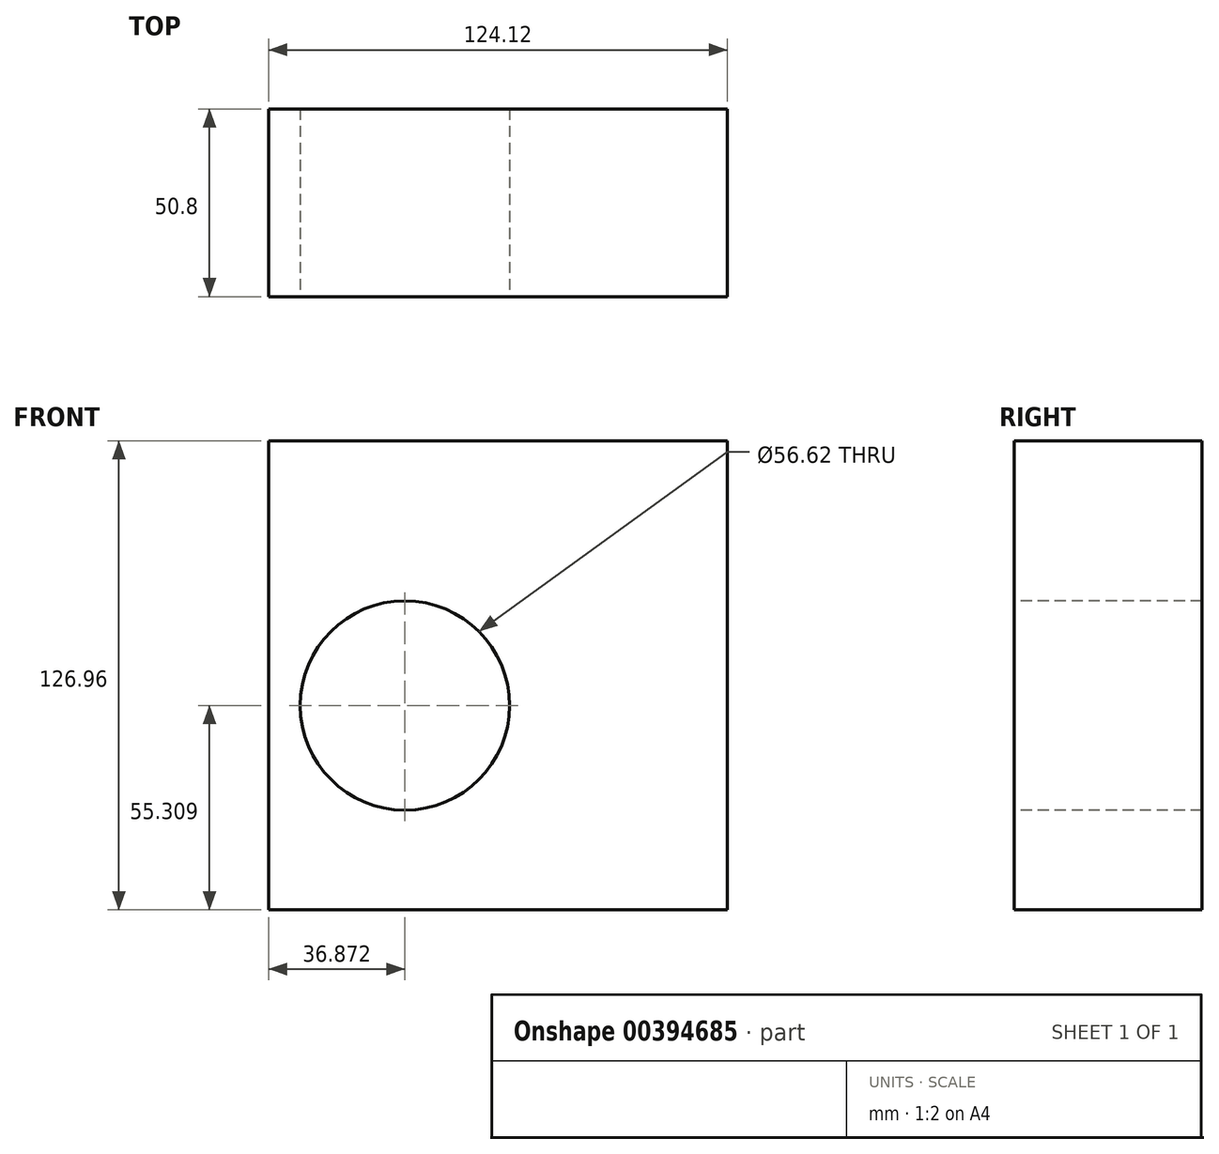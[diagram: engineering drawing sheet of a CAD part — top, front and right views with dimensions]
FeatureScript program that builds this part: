
annotation { "Feature Type Name" : "Feature", "Feature Type Description" : "" }
export const myFeature = defineFeature(function(context is Context, id is Id, definition is map)
    precondition{}
    {
        {
            var Q0;
            Q0=qCreatedBy(makeId("Front.planeOp"),FACE);
            var sketch = newSketch(context, id + "F0", { "sketchPlane" : qUnion([Q0])});
            skLineSegment(sketch, "E0.bottom", {"start": v(-62.06, 63.48) * mm, "end": v(62.06, 63.48) * mm});
            skLineSegment(sketch, "E0.top", {"start": v(-62.06, -63.48) * mm, "end": v(62.06, -63.48) * mm});
            skLineSegment(sketch, "E0.left", {"start": v(-62.06, 63.48) * mm, "end": v(-62.06, -63.48) * mm});
            skLineSegment(sketch, "E0.right", {"start": v(62.06, 63.48) * mm, "end": v(62.06, -63.48) * mm});
            skPoint(sketch, "E0.middle", {"position": v(0, 0) * mm});
            skSolve(sketch);
        }
        {
            var Q0;
            Q0=makeQuery(id+"F0.imprint","IMPRINT",FACE,{"disambiguationData":[TD([[makeQuery(id+"F0.imprint","IMPRINT",EDGE,{"derivedFrom":sQuery(id+"F0.wireOp",EDGE,"E0.bottom")}),-1.0]])]});
            extrude(context, id + "F1", {"entities" : qUnion([Q0]), "depth" : 76.2 * mm});
        }
        {
            var Q0;
            Q0=makeQuery(id+"F1.opExtrude","CAP_FACE",FACE,{"disambiguationData":[OSD([sQuery(id+"F0.wireOp",EDGE,"E0.bottom"),sQuery(id+"F0.wireOp",EDGE,"E0.top"),sQuery(id+"F0.wireOp",EDGE,"E0.left"),sQuery(id+"F0.wireOp",EDGE,"E0.right")])],"isStart":false});
            var sketch = newSketch(context, id + "F2", { "sketchPlane" : qUnion([Q0])});
            skCircle(sketch, "E1", {"center": v(-35.7, 36.61) * mm, "radius": 13.58 * mm});
            skCircle(sketch, "E2", {"center": v(0, 34.1) * mm, "radius": 8.09 * mm});
            skCircle(sketch, "E3", {"center": v(-25.19, -8.17) * mm, "radius": 28.31 * mm});
            skCircle(sketch, "E4", {"center": v(22.97, -9.2) * mm, "radius": 12.11 * mm});
            skCircle(sketch, "E5", {"center": v(34.5, 29.07) * mm, "radius": 23.09 * mm});
            skCircle(sketch, "E6", {"center": v(-44.86, -50.47) * mm, "radius": 6.88 * mm});
            skCircle(sketch, "E7", {"center": v(-14.68, -53.63) * mm, "radius": 4.76 * mm});
            skCircle(sketch, "E8", {"center": v(28.4, -47.3) * mm, "radius": 13.92 * mm});
            skCircle(sketch, "E9", {"center": v(50.78, -20.5) * mm, "radius": 8.55 * mm});
            skCircle(sketch, "E10", {"center": v(69.77, 53.83) * mm, "radius": 10.85 * mm});
            skCircle(sketch, "E11", {"center": v(94.52, 26.39) * mm, "radius": 10.15 * mm});
            skCircle(sketch, "E12", {"center": v(73.16, -1.48) * mm, "radius": 7.82 * mm});
            skCircle(sketch, "E13", {"center": v(77.57, -27.68) * mm, "radius": 2.6 * mm});
            skCircle(sketch, "E14", {"center": v(90.12, -8.12) * mm, "radius": 1.63 * mm});
            skCircle(sketch, "E15", {"center": v(93.85, 46.54) * mm, "radius": 1.66 * mm});
            skCircle(sketch, "E16", {"center": v(72.14, 32.47) * mm, "radius": 8.89 * mm});
            skCircle(sketch, "E17", {"center": v(88.08, 68.27) * mm, "radius": 9.28 * mm});
            skSolve(sketch);
        }
        {
            var Q0;
            Q0=makeQuery(id+"F2.imprint","IMPRINT",FACE,{"disambiguationData":[TD([[makeQuery(id+"F2.imprint","IMPRINT",EDGE,{"derivedFrom":sQuery(id+"F2.wireOp",EDGE,"E3")}),1.0]])]});
            extrude(context, id + "F3", {"entities" : qUnion([Q0]), "operationType" : NewBodyOperationType.REMOVE, "oppositeDirection" : true, "depth" : 243.6 * mm});
        }
        {
            var Q0;
            Q0=makeQuery(id+"F1.opExtrude","CAP_FACE",FACE,{"disambiguationData":[OSD([sQuery(id+"F0.wireOp",EDGE,"E0.bottom"),sQuery(id+"F0.wireOp",EDGE,"E0.top"),sQuery(id+"F0.wireOp",EDGE,"E0.left"),sQuery(id+"F0.wireOp",EDGE,"E0.right")])],"isStart":true});
            var sketch = newSketch(context, id + "F4", { "sketchPlane" : qUnion([Q0])});
            skFitSpline(sketch, "E18", {"points": [v(-57.07, 51) * mm, v(-58.02, -50.24) * mm, v(-48.73, -34.89) * mm, v(-39.63, -49.3) * mm, v(-38.68, 5.88) * mm, v(-30.34, -14.22) * mm, v(-35.45, -20.29) * mm, v(-22.75, -25.6) * mm, v(-32.61, -41.14) * mm, v(-26.35, -53.66) * mm, v(-23.13, -53.09) * mm, v(-15.93, -41.71) * mm, v(6.07, -54.04) * mm, v(11.57, -44.56) * mm, v(41.9, -53.85) * mm, v(54.8, -26.73) * mm, v(62.06, -25.22) * mm, v(57.45, -18.96) * mm, v(51, -27.11) * mm, v(44.37, -48.92) * mm, v(28.06, -43.23) * mm, v(6.26, -41.71) * mm, v(5.88, -47.59) * mm, v(-7.58, -33.75) * mm, v(-20.86, -39.44) * mm, v(-17.44, -31.28) * mm, v(-6.07, 11) * mm, v(20.29, 25.97) * mm, v(25.6, 26.92) * mm, v(41.52, 43.8) * mm, v(24.84, 44.93) * mm, v(0, 40) * mm, v(-3.98, 36.4) * mm, v(-6.83, 31.47) * mm, v(-12.7, 29.2) * mm, v(-15.17, 29.39) * mm, v(-27.87, 42.1) * mm, v(-57.07, 51) * mm]});
            skSolve(sketch);
        }
        {
            var Q0;
            {var subQ0=sQuery(id+"F4.wireOp",EDGE,"E18");var subQ1=makeQuery(id+"F1.opExtrude","CAP_EDGE",EDGE,{"disambiguationData":[OSD([sQuery(id+"F0.wireOp",EDGE,"E0.right")])],"isStart":true});var subQ2=makeQuery(id+"F4.imprint","INTERSECT",VERTEX,{"disambiguationData":[OD(0.0)],"derivedFrom":[subQ1,subQ0]});Q0=makeQuery(id+"F4.imprint","IMPRINT",FACE,{"disambiguationData":[TD([[makeQuery(id+"F4.imprint","IMPRINT",EDGE,{"disambiguationData":[TD([[subQ2,-1.0]])],"derivedFrom":subQ0}),1.0]])]});}
            var sketch = newSketch(context, id + "F5", { "sketchPlane" : qUnion([Q0])});
            skSolve(sketch);
        }
        {
            var Q0;
            {var subQ0=sQuery(id+"F4.wireOp",EDGE,"E18");var subQ1=makeQuery(id+"F1.opExtrude","CAP_EDGE",EDGE,{"disambiguationData":[OSD([sQuery(id+"F0.wireOp",EDGE,"E0.right")])],"isStart":true});var subQ2=makeQuery(id+"F4.imprint","INTERSECT",VERTEX,{"disambiguationData":[OD(0.0)],"derivedFrom":[subQ1,subQ0]});Q0=makeQuery(id+"F5.imprint","IMPRINT",FACE,{"disambiguationData":[TD([[makeQuery(id+"F5.imprint","IMPRINT",EDGE,{"derivedFrom":makeQuery(id+"F4.imprint","IMPRINT",EDGE,{"disambiguationData":[TD([[subQ2,-1.0]])],"derivedFrom":subQ0})}),1.0]])]});}
            var Q1;
            Q1=makeQuery(id+"F1.opExtrude","CAP_FACE",FACE,{"disambiguationData":[OSD([sQuery(id+"F0.wireOp",EDGE,"E0.bottom"),sQuery(id+"F0.wireOp",EDGE,"E0.top"),sQuery(id+"F0.wireOp",EDGE,"E0.left"),sQuery(id+"F0.wireOp",EDGE,"E0.right")])],"isStart":true});
            var Q2;
            Q2=makeQuery(id+"F1.opExtrude","CAP_FACE",FACE,{"disambiguationData":[OSD([sQuery(id+"F0.wireOp",EDGE,"E0.bottom"),sQuery(id+"F0.wireOp",EDGE,"E0.top"),sQuery(id+"F0.wireOp",EDGE,"E0.left"),sQuery(id+"F0.wireOp",EDGE,"E0.right")])],"isStart":false});
            extrude(context, id + "F6", {"entities" : qUnion([Q0, Q1, Q2]), "operationType" : NewBodyOperationType.REMOVE, "oppositeDirection" : true, "depth" : 25.4 * mm});
        }
    });
